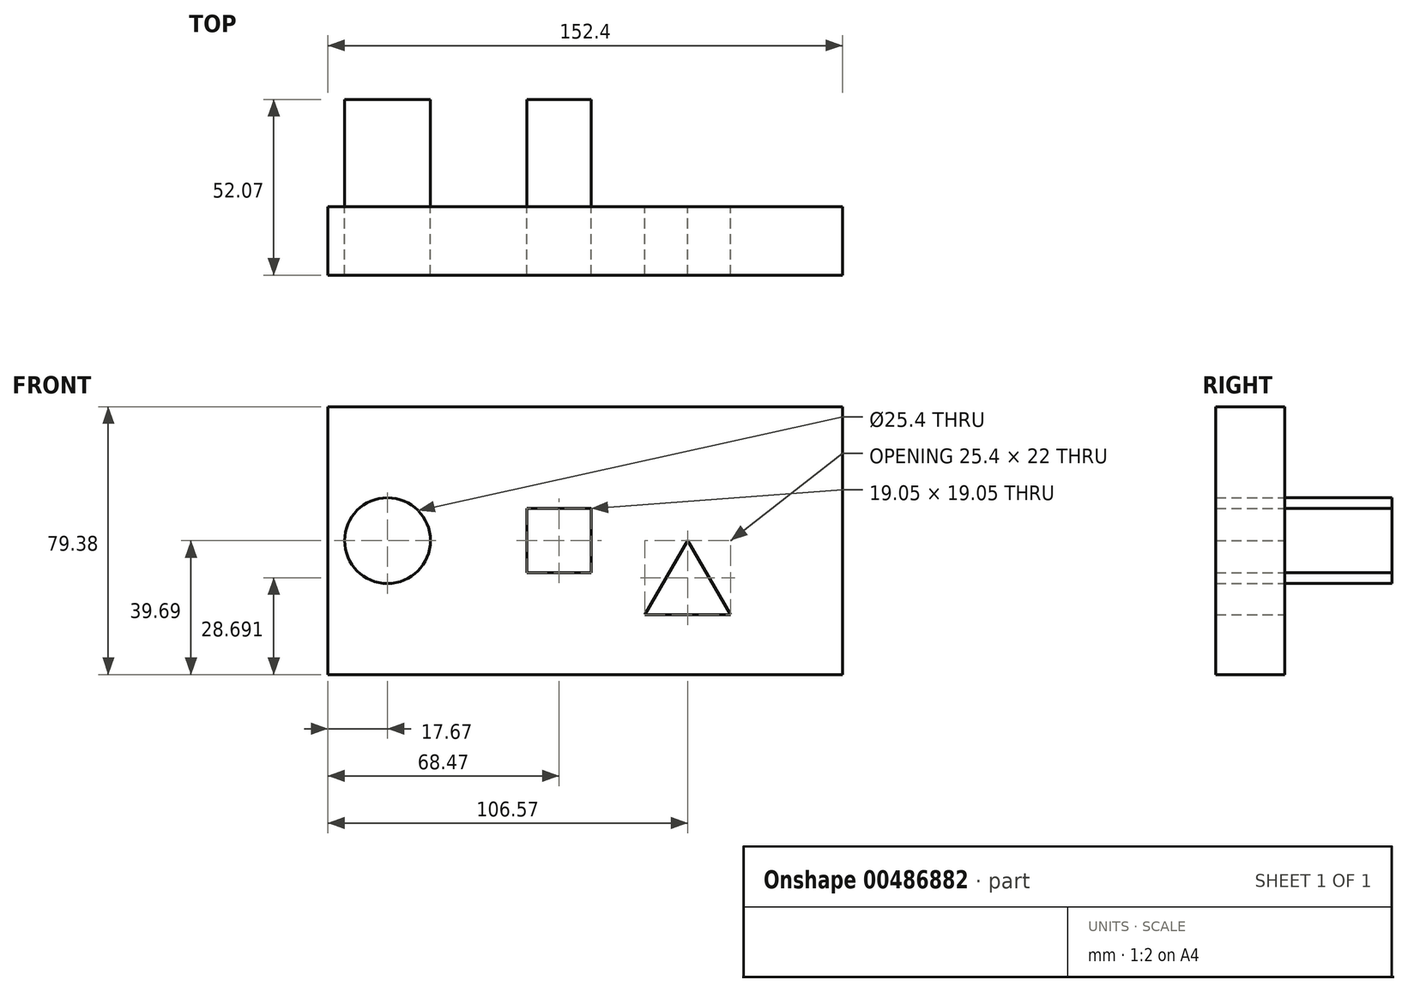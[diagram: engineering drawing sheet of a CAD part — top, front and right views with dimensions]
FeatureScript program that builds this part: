
annotation { "Feature Type Name" : "Feature", "Feature Type Description" : "" }
export const myFeature = defineFeature(function(context is Context, id is Id, definition is map)
    precondition{}
    {
        {
            var Q0;
            Q0=qCreatedBy(makeId("Front.planeOp"),FACE);
            var sketch = newSketch(context, id + "F0", { "sketchPlane" : qUnion([Q0])});
            skPoint(sketch, "E0.middle", {"position": v(0, 0) * mm});
            skLineSegment(sketch, "E1", {"start": v(6.35, 0) * mm, "end": v(-6.35, -22) * mm});
            skLineSegment(sketch, "E2", {"start": v(-6.35, -22) * mm, "end": v(19.05, -22) * mm});
            skLineSegment(sketch, "E3", {"start": v(6.35, 0) * mm, "end": v(19.05, -22) * mm});
            skLineSegment(sketch, "E4.bottom", {"start": v(-22.22, -9.53) * mm, "end": v(-41.27, -9.52) * mm});
            skLineSegment(sketch, "E4.top", {"start": v(-22.23, 9.53) * mm, "end": v(-41.28, 9.53) * mm});
            skLineSegment(sketch, "E4.left", {"start": v(-22.22, -9.53) * mm, "end": v(-22.23, 9.52) * mm});
            skLineSegment(sketch, "E4.right", {"start": v(-41.28, -9.52) * mm, "end": v(-41.28, 9.53) * mm});
            skPoint(sketch, "E4.middle", {"position": v(-31.75, 0) * mm});
            skPoint(sketch, "E5", {"position": v(52.18, -39.69) * mm});
            skPoint(sketch, "E6", {"position": v(0, -39.69) * mm});
            skPoint(sketch, "E7", {"position": v(-100.22, -39.69) * mm});
            skLineSegment(sketch, "E8", {"start": v(-100.22, -39.69) * mm, "end": v(52.18, -39.69) * mm});
            skPoint(sketch, "E9", {"position": v(-24.02, -39.69) * mm});
            skLineSegment(sketch, "E10.bottom", {"start": v(52.18, -39.69) * mm, "end": v(-100.22, -39.69) * mm});
            skLineSegment(sketch, "E10.top", {"start": v(52.18, 39.69) * mm, "end": v(-100.22, 39.69) * mm});
            skLineSegment(sketch, "E10.left", {"start": v(52.18, -39.69) * mm, "end": v(52.18, 39.69) * mm});
            skLineSegment(sketch, "E10.right", {"start": v(-100.22, -39.69) * mm, "end": v(-100.22, 39.69) * mm});
            skPoint(sketch, "E10.middle", {"position": v(-24.02, 0) * mm});
            skCircle(sketch, "E11", {"center": v(-82.55, 0) * mm, "radius": 12.7 * mm});
            skSolve(sketch);
        }
        {
            var Q0;
            Q0 = qSketchRegion(id + "F0", true);
            var Q1;
            Q1=makeQuery(id+"F0.imprint","IMPRINT",FACE,{"disambiguationData":[TD([[makeQuery(id+"F0.imprint","IMPRINT",EDGE,{"derivedFrom":sQuery(id+"F0.wireOp",EDGE,"E1")}),-1.0]])]});
            extrude(context, id + "F1", {"entities" : qUnion([Q0, Q1]), "depth" : 20.32 * mm});
        }
        {
            var Q0;
            Q0=makeQuery(id+"F0.imprint","IMPRINT",FACE,{"disambiguationData":[TD([[makeQuery(id+"F0.imprint","IMPRINT",EDGE,{"derivedFrom":sQuery(id+"F0.wireOp",EDGE,"E4.bottom")}),-1.0]])]});
            extrude(context, id + "F2", {"entities" : qUnion([Q0]), "operationType" : NewBodyOperationType.ADD, "oppositeDirection" : true, "depth" : 31.75 * mm});
        }
        {
            var Q0;
            Q0=makeQuery(id+"F0.imprint","IMPRINT",FACE,{"disambiguationData":[TD([[makeQuery(id+"F0.imprint","IMPRINT",EDGE,{"derivedFrom":sQuery(id+"F0.wireOp",EDGE,"E11")}),1.0]])]});
            extrude(context, id + "F3", {"entities" : qUnion([Q0]), "operationType" : NewBodyOperationType.ADD, "oppositeDirection" : true, "depth" : 31.75 * mm});
        }
        {
            var Q0;
            Q0=makeQuery(id+"F3.opExtrude","CAP_FACE",FACE,{"disambiguationData":[OSD([sQuery(id+"F0.wireOp",EDGE,"E11")])],"isStart":true});
            extrude(context, id + "F4", {"entities" : qUnion([Q0]), "depth" : 20.32 * mm});
        }
    });
